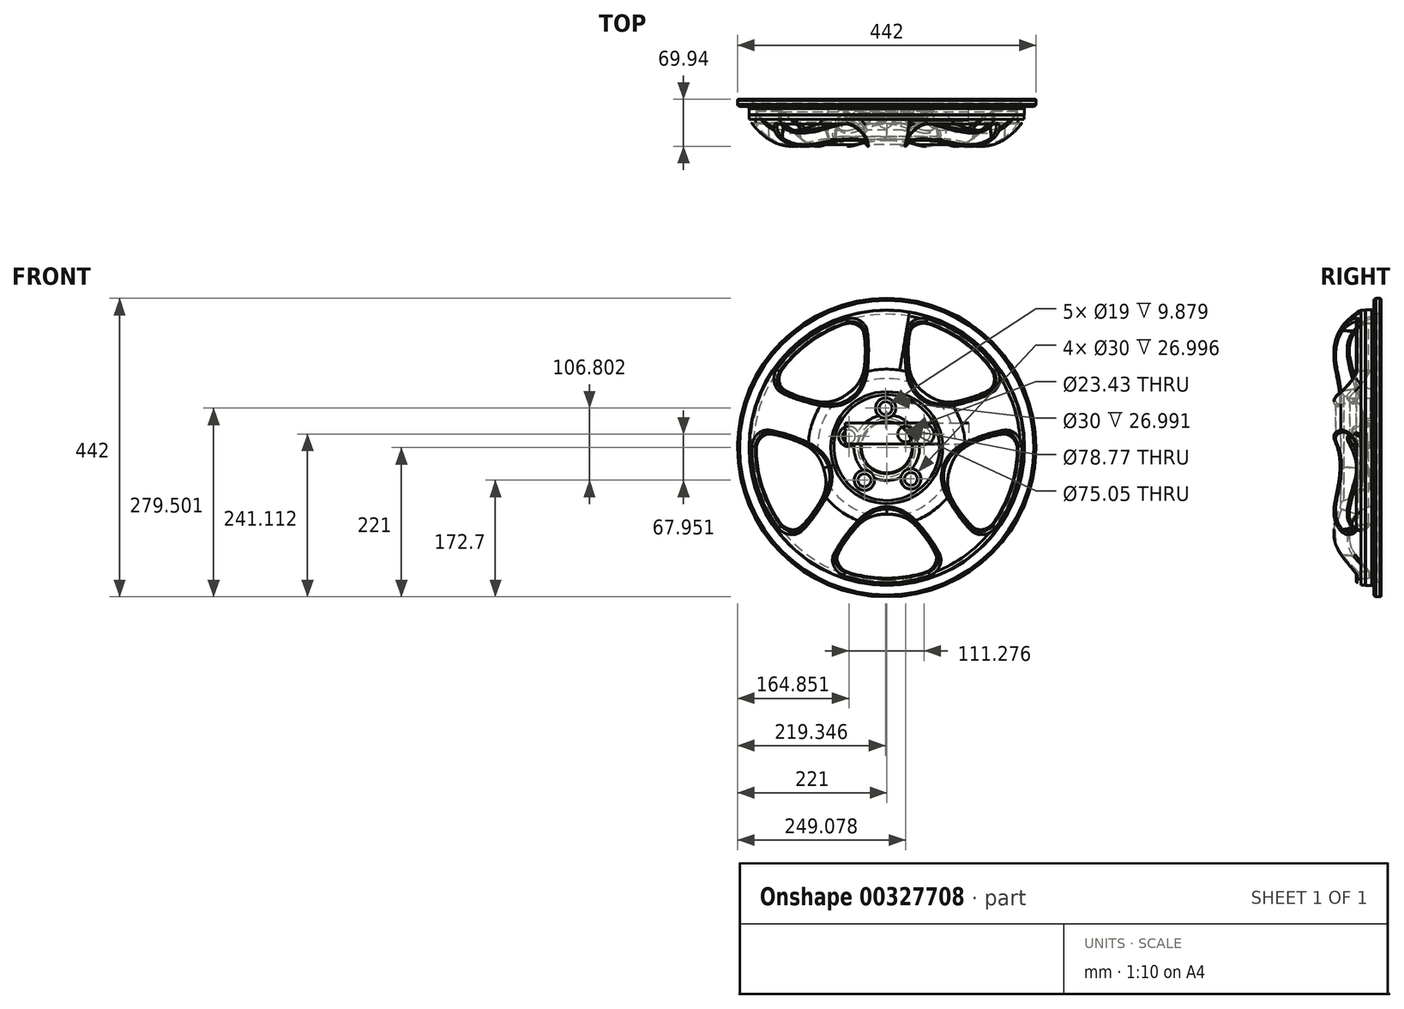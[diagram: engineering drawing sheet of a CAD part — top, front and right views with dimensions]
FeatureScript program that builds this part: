
annotation { "Feature Type Name" : "Feature", "Feature Type Description" : "" }
export const myFeature = defineFeature(function(context is Context, id is Id, definition is map)
    precondition{}
    {
        {
            var Q0;
            Q0=qCreatedBy(makeId("Right.planeOp"),FACE);
            var sketch = newSketch(context, id + "F0", { "sketchPlane" : qUnion([Q0])});
            skLineSegment(sketch, "E0", {"start": v(-299.05, 0) * mm, "end": v(298.01, 0) * mm, "construction": true});
            skLineSegment(sketch, "E1", {"start": v(-4.21, 217.93) * mm, "end": v(-4.21, 208.07) * mm});
            skFitSpline(sketch, "E2", {"points": [v(-4.21, 208.07) * mm, v(-7.55, 204.04) * mm], "startDerivative": vector(0, -5.98) * mm, "endDerivative": vector(-7.66, -0.8) * mm});
            skLineSegment(sketch, "E3", {"start": v(-7.55, 204.04) * mm, "end": v(-16.4, 204.04) * mm});
            skLineSegment(sketch, "E4", {"start": v(-16.4, 204.04) * mm, "end": v(-17.3, 203.46) * mm});
            skLineSegment(sketch, "E5", {"start": v(-17.3, 203.46) * mm, "end": v(-23.41, 203.46) * mm});
            skFitSpline(sketch, "E6", {"points": [v(-23.41, 203.46) * mm, v(-60.74, 116.16) * mm], "startDerivative": vector(-154.66, -86.95) * mm, "endDerivative": vector(7.16, -35.8) * mm});
            skLineSegment(sketch, "E7", {"start": v(-60.74, 116.16) * mm, "end": v(-53.35, 82.9) * mm});
            skFitSpline(sketch, "E8", {"points": [v(-53.35, 82.9) * mm, v(-48.78, 78.17) * mm], "startDerivative": vector(1.61, -7.86) * mm, "endDerivative": vector(6.32, -3.9) * mm});
            skFitSpline(sketch, "E9", {"points": [v(-48.78, 78.17) * mm, v(-19.88, 48.61) * mm], "startDerivative": vector(35.95, -13.03) * mm, "endDerivative": vector(3.82, -62.67) * mm});
            skLineSegment(sketch, "E10", {"start": v(-19.88, 48.61) * mm, "end": v(-19.88, 0) * mm});
            skFitSpline(sketch, "E11", {"points": [v(-4.21, 217.93) * mm, v(-1.18, 221) * mm], "startDerivative": vector(0.76, 5.98) * mm, "endDerivative": vector(4.44, 0.8) * mm});
            skLineSegment(sketch, "E12", {"start": v(-1.18, 221) * mm, "end": v(4.33, 221) * mm});
            skFitSpline(sketch, "E13", {"points": [v(4.33, 221) * mm, v(6.34, 219.66) * mm], "startDerivative": vector(2.69, 0.13) * mm, "endDerivative": vector(0.27, -2.69) * mm});
            skLineSegment(sketch, "E14", {"start": v(6.34, 219.66) * mm, "end": v(6.34, 201.82) * mm});
            skLineSegment(sketch, "E15", {"start": v(6.34, 201.82) * mm, "end": v(0, 197.57) * mm});
            skFitSpline(sketch, "E16", {"points": [v(0, 197.57) * mm, v(-39.64, 134.42) * mm], "startDerivative": vector(-50.19, -12.62) * mm, "endDerivative": vector(20.32, -117.94) * mm});
            skFitSpline(sketch, "E17", {"points": [v(-39.64, 134.42) * mm, v(-30.1, 102.27) * mm], "startDerivative": vector(9.9, -56.41) * mm, "endDerivative": vector(11.18, -25.2) * mm});
            skFitSpline(sketch, "E18", {"points": [v(-30.1, 102.27) * mm, v(-2.1, 84.7) * mm], "startDerivative": vector(23.3, -39.79) * mm, "endDerivative": vector(30.8, -8.12) * mm});
            skFitSpline(sketch, "E19", {"points": [v(-2.1, 84.7) * mm, v(0, 83.48) * mm], "startDerivative": vector(2.56, -0.67) * mm, "endDerivative": vector(0.96, -2.28) * mm});
            skLineSegment(sketch, "E20", {"start": v(0, 83.48) * mm, "end": v(0, 0) * mm});
            skLineSegment(sketch, "E21", {"start": v(0, 0) * mm, "end": v(-19.88, 0) * mm});
            skLineSegment(sketch, "E22", {"start": v(0, -290.73) * mm, "end": v(0, 298.47) * mm, "construction": true});
            skSolve(sketch);
        }
        {
            var Q0;
            Q0 = qSketchRegion(id + "F0", true);
            var Q1;
            Q1=sQuery(id+"F0.wireOp",EDGE,"E0");
            revolve(context, id + "F1", {"entities" : qUnion([Q0]), "axis" : qUnion([Q1]), "revolveType" : RevolveType.FULL});
        }
        {
            var Q0;
            Q0=qCreatedBy(makeId("Front.planeOp"),FACE);
            cPlane(context, id + "F2", {"entities" : qUnion([Q0]), "cplaneType" : CPlaneType.OFFSET, "offset" : 64.3 * mm, "width" : 150 * mm, "height" : 150 * mm});
        }
        {
            var Q0;
            Q0=qCreatedBy(makeId("Front.planeOp"),FACE);
            cPlane(context, id + "F3", {"entities" : qUnion([Q0]), "cplaneType" : CPlaneType.OFFSET, "offset" : 10 * mm, "width" : 150 * mm, "height" : 150 * mm});
        }
        {
            var Q0;
            Q0=qCreatedBy(makeId("Front.planeOp"),FACE);
            cPlane(context, id + "F4", {"entities" : qUnion([Q0]), "cplaneType" : CPlaneType.OFFSET, "offset" : 83 * mm, "width" : 150 * mm, "height" : 150 * mm});
        }
        {
            var Q0;
            Q0=qCreatedBy(makeId("Front.planeOp"),FACE);
            cPlane(context, id + "F5", {"entities" : qUnion([Q0]), "cplaneType" : CPlaneType.OFFSET, "offset" : 5 * mm, "width" : 150 * mm, "height" : 150 * mm});
        }
        {
            var Q0;
            Q0=qCreatedBy(id+"F4.planeOp",FACE);
            var sketch = newSketch(context, id + "F6", { "sketchPlane" : qUnion([Q0])});
            skLineSegment(sketch, "E23", {"start": v(-344.65, 0) * mm, "end": v(353.31, 0) * mm, "construction": true});
            skLineSegment(sketch, "E24", {"start": v(0, -300.82) * mm, "end": v(0, 297.65) * mm, "construction": true});
            skFitSpline(sketch, "E25", {"points": [v(-79, -157.26) * mm, v(-39.94, -107.29) * mm], "startDerivative": vector(39.24, 57.85) * mm, "endDerivative": vector(46.78, 52.32) * mm});
            skFitSpline(sketch, "E26", {"points": [v(-39.94, -107.29) * mm, v(0, -84.82) * mm], "startDerivative": vector(39.74, 44.77) * mm, "endDerivative": vector(30.47, -1.33) * mm});
            skFitSpline(sketch, "E27", {"points": [v(-79, -157.26) * mm, v(-77.15, -185.64) * mm], "startDerivative": vector(-20, -29.16) * mm, "endDerivative": vector(24.22, -15.46) * mm});
            skArc(sketch, "E28", {"start": v(-77.15, -185.64) * mm, "mid": v(-39.33, -197.14) * mm, "end": v(0, -201.03) * mm});
            skFitSpline(sketch, "E29.MirrorCS", {"points": [v(39.94, -107.29) * mm, v(0, -84.82) * mm], "startDerivative": vector(-39.74, 44.77) * mm, "endDerivative": vector(-30.47, -1.33) * mm});
            skFitSpline(sketch, "E30.MirrorCS", {"points": [v(79, -157.26) * mm, v(39.94, -107.29) * mm], "startDerivative": vector(-39.24, 57.85) * mm, "endDerivative": vector(-46.78, 52.32) * mm});
            skFitSpline(sketch, "E31.MirrorCS", {"points": [v(79, -157.26) * mm, v(77.15, -185.64) * mm], "startDerivative": vector(20, -29.16) * mm, "endDerivative": vector(-24.22, -15.46) * mm});
            skArc(sketch, "E32.MirrorCS", {"start": v(77.15, -185.64) * mm, "mid": v(39.33, -197.14) * mm, "end": v(0, -201.03) * mm});
            skLineSegment(sketch, "E33", {"start": v(-106.5, -327.78) * mm, "end": v(109.18, 336.02) * mm, "construction": true});
            skLineSegment(sketch, "E34", {"start": v(286.1, -92.96) * mm, "end": v(-283.08, 91.98) * mm, "construction": true});
            skFitSpline(sketch, "E35", {"points": [v(125.15, -123.74) * mm, v(89.7, -71.14) * mm], "startDerivative": vector(-42.9, 55.2) * mm, "endDerivative": vector(-35.3, 60.66) * mm});
            skFitSpline(sketch, "E36", {"points": [v(89.7, -71.14) * mm, v(80.67, -26.21) * mm], "startDerivative": vector(-30.3, 51.63) * mm, "endDerivative": vector(10.52, 31.68) * mm});
            skFitSpline(sketch, "E37", {"points": [v(125.15, -123.74) * mm, v(152.71, -130.73) * mm], "startDerivative": vector(21.56, -28.03) * mm, "endDerivative": vector(22.19, 18.26) * mm});
            skArc(sketch, "E38", {"start": v(152.71, -130.73) * mm, "mid": v(175.34, -98.33) * mm, "end": v(191.19, -62.12) * mm});
            skFitSpline(sketch, "E39.MirrorCS", {"points": [v(114.38, 4.83) * mm, v(80.67, -26.21) * mm], "startDerivative": vector(-54.86, -23.96) * mm, "endDerivative": vector(-10.11, -31.81) * mm});
            skFitSpline(sketch, "E40.MirrorCS", {"points": [v(173.98, 26.55) * mm, v(114.38, 4.83) * mm], "startDerivative": vector(-67.15, -19.44) * mm, "endDerivative": vector(-64.22, -28.33) * mm});
            skFitSpline(sketch, "E41.MirrorCS", {"points": [v(173.98, 26.55) * mm, v(200.39, 16) * mm], "startDerivative": vector(33.92, 10) * mm, "endDerivative": vector(7.22, -27.81) * mm});
            skArc(sketch, "E42.MirrorCS", {"start": v(200.39, 16) * mm, "mid": v(199.65, -23.51) * mm, "end": v(191.19, -62.12) * mm});
            skLineSegment(sketch, "E43", {"start": v(278.83, -202.58) * mm, "end": v(-285.84, 207.67) * mm, "construction": true});
            skLineSegment(sketch, "E44", {"start": v(176.82, 243.37) * mm, "end": v(-174.95, -240.8) * mm, "construction": true});
            skFitSpline(sketch, "E45", {"points": [v(156.35, 80.79) * mm, v(95.37, 63.32) * mm], "startDerivative": vector(-65.75, -23.74) * mm, "endDerivative": vector(-68.6, -14.83) * mm});
            skFitSpline(sketch, "E46", {"points": [v(95.37, 63.32) * mm, v(49.85, 68.62) * mm], "startDerivative": vector(-58.47, -12.86) * mm, "endDerivative": vector(-24.62, 18.84) * mm});
            skFitSpline(sketch, "E47", {"points": [v(156.35, 80.79) * mm, v(171.53, 104.84) * mm], "startDerivative": vector(33.32, 11.84) * mm, "endDerivative": vector(-10.5, 26.74) * mm});
            skArc(sketch, "E48", {"start": v(171.53, 104.84) * mm, "mid": v(147.7, 136.37) * mm, "end": v(118.16, 162.63) * mm});
            skFitSpline(sketch, "E49.MirrorCS", {"points": [v(30.75, 110.27) * mm, v(49.85, 68.62) * mm], "startDerivative": vector(5.84, -59.58) * mm, "endDerivative": vector(25.53, -17.6) * mm});
            skFitSpline(sketch, "E50.MirrorCS", {"points": [v(28.52, 173.67) * mm, v(30.75, 110.27) * mm], "startDerivative": vector(-2.26, -69.87) * mm, "endDerivative": vector(7.1, -69.83) * mm});
            skFitSpline(sketch, "E51.MirrorCS", {"points": [v(28.52, 173.67) * mm, v(46.7, 195.53) * mm], "startDerivative": vector(0.97, 35.35) * mm, "endDerivative": vector(28.68, -1.73) * mm});
            skArc(sketch, "E52.MirrorCS", {"start": v(46.7, 195.53) * mm, "mid": v(84.06, 182.6) * mm, "end": v(118.16, 162.63) * mm});
            skLineSegment(sketch, "E53", {"start": v(278.83, 202.58) * mm, "end": v(-285.84, -207.67) * mm, "construction": true});
            skLineSegment(sketch, "E54", {"start": v(-176.82, 243.37) * mm, "end": v(174.95, -240.8) * mm, "construction": true});
            skFitSpline(sketch, "E55", {"points": [v(-28.52, 173.67) * mm, v(-30.75, 110.27) * mm], "startDerivative": vector(2.26, -69.87) * mm, "endDerivative": vector(-7.1, -69.83) * mm});
            skFitSpline(sketch, "E56", {"points": [v(-30.75, 110.27) * mm, v(-49.85, 68.62) * mm], "startDerivative": vector(-5.84, -59.58) * mm, "endDerivative": vector(-29.1, -20.37) * mm});
            skFitSpline(sketch, "E57", {"points": [v(-28.52, 173.67) * mm, v(-46.7, 195.53) * mm], "startDerivative": vector(-0.97, 35.35) * mm, "endDerivative": vector(-28.68, -1.73) * mm});
            skArc(sketch, "E58", {"start": v(-46.7, 195.53) * mm, "mid": v(-84.06, 182.6) * mm, "end": v(-118.16, 162.63) * mm});
            skFitSpline(sketch, "E59.MirrorCS", {"points": [v(-95.37, 63.32) * mm, v(-49.85, 68.62) * mm], "startDerivative": vector(58.47, -12.86) * mm, "endDerivative": vector(28.37, 21.39) * mm});
            skFitSpline(sketch, "E60.MirrorCS", {"points": [v(-156.35, 80.79) * mm, v(-95.37, 63.32) * mm], "startDerivative": vector(65.75, -23.74) * mm, "endDerivative": vector(68.6, -14.83) * mm});
            skFitSpline(sketch, "E61.MirrorCS", {"points": [v(-156.35, 80.79) * mm, v(-171.53, 104.84) * mm], "startDerivative": vector(-33.32, 11.84) * mm, "endDerivative": vector(10.5, 26.74) * mm});
            skArc(sketch, "E62.MirrorCS", {"start": v(-171.53, 104.84) * mm, "mid": v(-147.7, 136.37) * mm, "end": v(-118.16, 162.63) * mm});
            skLineSegment(sketch, "E63", {"start": v(-106.5, 327.78) * mm, "end": v(109.18, -336.02) * mm, "construction": true});
            skLineSegment(sketch, "E64", {"start": v(-286.1, -92.96) * mm, "end": v(283.08, 91.98) * mm, "construction": true});
            skFitSpline(sketch, "E65", {"points": [v(-173.98, 26.55) * mm, v(-114.38, 4.83) * mm], "startDerivative": vector(67.15, -19.44) * mm, "endDerivative": vector(64.22, -28.33) * mm});
            skFitSpline(sketch, "E66", {"points": [v(-114.38, 4.83) * mm, v(-80.67, -26.21) * mm], "startDerivative": vector(54.86, -23.96) * mm, "endDerivative": vector(8.83, -29.97) * mm});
            skFitSpline(sketch, "E67", {"points": [v(-173.98, 26.55) * mm, v(-200.39, 16) * mm], "startDerivative": vector(-33.92, 10) * mm, "endDerivative": vector(-7.22, -27.81) * mm});
            skArc(sketch, "E68", {"start": v(-200.39, 16) * mm, "mid": v(-199.65, -23.51) * mm, "end": v(-191.19, -62.12) * mm});
            skFitSpline(sketch, "E69.MirrorCS", {"points": [v(-89.7, -71.14) * mm, v(-80.67, -26.21) * mm], "startDerivative": vector(30.3, 51.63) * mm, "endDerivative": vector(-10.47, 29.44) * mm});
            skFitSpline(sketch, "E70.MirrorCS", {"points": [v(-125.15, -123.74) * mm, v(-89.7, -71.14) * mm], "startDerivative": vector(42.9, 55.2) * mm, "endDerivative": vector(35.3, 60.66) * mm});
            skFitSpline(sketch, "E71.MirrorCS", {"points": [v(-125.15, -123.74) * mm, v(-152.71, -130.73) * mm], "startDerivative": vector(-21.56, -28.03) * mm, "endDerivative": vector(-22.19, 18.26) * mm});
            skArc(sketch, "E72.MirrorCS", {"start": v(-152.71, -130.73) * mm, "mid": v(-175.34, -98.33) * mm, "end": v(-191.19, -62.12) * mm});
            skCircle(sketch, "E73", {"center": v(0, 0) * mm, "radius": 225 * mm});
            skSolve(sketch);
        }
        {
            var Q0;
            Q0=qCreatedBy(id+"F5.planeOp",FACE);
            var sketch = newSketch(context, id + "F7", { "sketchPlane" : qUnion([Q0])});
            skFitSpline(sketch, "E74", {"points": [v(0, -103.08) * mm, v(-47.4, -124.7) * mm], "startDerivative": vector(-28.83, 0.66) * mm, "endDerivative": vector(-54.4, -62.91) * mm});
            skFitSpline(sketch, "E75", {"points": [v(-47.4, -124.7) * mm, v(-70.45, -161.6) * mm], "startDerivative": vector(-29.51, -36.76) * mm, "endDerivative": vector(-18.84, -39.87) * mm});
            skFitSpline(sketch, "E76", {"points": [v(-70.45, -161.6) * mm, v(-58.17, -183.99) * mm], "startDerivative": vector(-6.13, -31.47) * mm, "endDerivative": vector(23.73, -8.28) * mm});
            skArc(sketch, "E77", {"start": v(-58.17, -183.99) * mm, "mid": v(-29.43, -190.7) * mm, "end": v(0, -192.96) * mm});
            skFitSpline(sketch, "E78.MirrorCS", {"points": [v(0, -103.08) * mm, v(47.4, -124.7) * mm], "startDerivative": vector(28.83, 0.66) * mm, "endDerivative": vector(54.4, -62.91) * mm});
            skFitSpline(sketch, "E79.MirrorCS", {"points": [v(47.4, -124.7) * mm, v(70.45, -161.6) * mm], "startDerivative": vector(29.51, -36.76) * mm, "endDerivative": vector(18.84, -39.87) * mm});
            skFitSpline(sketch, "E80.MirrorCS", {"points": [v(70.45, -161.6) * mm, v(58.17, -183.99) * mm], "startDerivative": vector(6.13, -31.47) * mm, "endDerivative": vector(-23.73, -8.28) * mm});
            skArc(sketch, "E81.MirrorCS", {"start": v(58.17, -183.99) * mm, "mid": v(29.43, -190.7) * mm, "end": v(0, -192.96) * mm});
            skLineSegment(sketch, "E82", {"start": v(0, 310.72) * mm, "end": v(0, -319.36) * mm, "construction": true});
            skLineSegment(sketch, "E83", {"start": v(362.48, 0) * mm, "end": v(-377.5, 0) * mm, "construction": true});
            skFitSpline(sketch, "E84", {"points": [v(-98.04, -31.85) * mm, v(-133.25, 6.54) * mm], "startDerivative": vector(-8.29, 27.62) * mm, "endDerivative": vector(-76.64, 32.29) * mm});
            skFitSpline(sketch, "E85", {"points": [v(-133.25, 6.54) * mm, v(-175.46, 17.06) * mm], "startDerivative": vector(-44.08, 16.7) * mm, "endDerivative": vector(-43.74, 5.6) * mm});
            skFitSpline(sketch, "E86", {"points": [v(-175.46, 17.06) * mm, v(-192.96, -1.53) * mm], "startDerivative": vector(-31.83, -3.9) * mm, "endDerivative": vector(-0.54, -25.12) * mm});
            skArc(sketch, "E87", {"start": v(-192.96, -1.53) * mm, "mid": v(-190.46, -30.94) * mm, "end": v(-183.52, -59.63) * mm});
            skFitSpline(sketch, "E88.MirrorCS", {"points": [v(-98.04, -31.85) * mm, v(-103.96, -83.62) * mm], "startDerivative": vector(9.53, -27.22) * mm, "endDerivative": vector(-43.02, -71.17) * mm});
            skFitSpline(sketch, "E89.MirrorCS", {"points": [v(-103.96, -83.62) * mm, v(-131.92, -116.93) * mm], "startDerivative": vector(-25.84, -39.43) * mm, "endDerivative": vector(-32.1, -30.24) * mm});
            skFitSpline(sketch, "E90.MirrorCS", {"points": [v(-131.92, -116.93) * mm, v(-157, -112.18) * mm], "startDerivative": vector(-28.04, -15.56) * mm, "endDerivative": vector(-15.2, 20) * mm});
            skArc(sketch, "E91.MirrorCS", {"start": v(-157, -112.18) * mm, "mid": v(-172.28, -86.92) * mm, "end": v(-183.52, -59.63) * mm});
            skLineSegment(sketch, "E92", {"start": v(295.52, 96.02) * mm, "end": v(-303.73, -98.69) * mm, "construction": true});
            skLineSegment(sketch, "E93", {"start": v(112.01, -344.74) * mm, "end": v(-116.65, 359.02) * mm, "construction": true});
            skLineSegment(sketch, "E94.0", {"start": v(0, 0) * mm, "end": v(112.01, -344.74) * mm, "construction": true});
            skLineSegment(sketch, "E95.0", {"start": v(0, 0) * mm, "end": v(295.52, 96.02) * mm, "construction": true});
            skFitSpline(sketch, "E96", {"points": [v(98.04, -31.85) * mm, v(103.96, -83.62) * mm], "startDerivative": vector(-9.53, -27.22) * mm, "endDerivative": vector(43.02, -71.17) * mm});
            skFitSpline(sketch, "E97", {"points": [v(103.96, -83.62) * mm, v(131.92, -116.93) * mm], "startDerivative": vector(25.84, -39.43) * mm, "endDerivative": vector(32.1, -30.24) * mm});
            skFitSpline(sketch, "E98", {"points": [v(131.92, -116.93) * mm, v(157, -112.18) * mm], "startDerivative": vector(28.04, -15.56) * mm, "endDerivative": vector(15.2, 20) * mm});
            skArc(sketch, "E99", {"start": v(157, -112.18) * mm, "mid": v(172.28, -86.92) * mm, "end": v(183.52, -59.63) * mm});
            skFitSpline(sketch, "E100.MirrorCS", {"points": [v(98.04, -31.85) * mm, v(133.25, 6.54) * mm], "startDerivative": vector(8.29, 27.62) * mm, "endDerivative": vector(76.64, 32.29) * mm});
            skFitSpline(sketch, "E101.MirrorCS", {"points": [v(133.25, 6.54) * mm, v(175.46, 17.06) * mm], "startDerivative": vector(44.08, 16.7) * mm, "endDerivative": vector(43.74, 5.6) * mm});
            skFitSpline(sketch, "E102.MirrorCS", {"points": [v(175.46, 17.06) * mm, v(192.96, -1.53) * mm], "startDerivative": vector(31.83, -3.9) * mm, "endDerivative": vector(0.54, -25.12) * mm});
            skArc(sketch, "E103.MirrorCS", {"start": v(192.96, -1.53) * mm, "mid": v(190.46, -30.94) * mm, "end": v(183.52, -59.63) * mm});
            skLineSegment(sketch, "E104", {"start": v(-295.52, 96.02) * mm, "end": v(303.73, -98.69) * mm, "construction": true});
            skLineSegment(sketch, "E105", {"start": v(112.01, 344.74) * mm, "end": v(-116.65, -359.02) * mm, "construction": true});
            skLineSegment(sketch, "E106.0", {"start": v(0, 0) * mm, "end": v(112.01, 344.74) * mm, "construction": true});
            skLineSegment(sketch, "E107.0", {"start": v(0, 0) * mm, "end": v(-295.52, 96.02) * mm, "construction": true});
            skFitSpline(sketch, "E108", {"points": [v(60.6, 83.4) * mm, v(111.65, 73.03) * mm], "startDerivative": vector(22.94, -17.48) * mm, "endDerivative": vector(80.98, 18.93) * mm});
            skFitSpline(sketch, "E109", {"points": [v(111.65, 73.03) * mm, v(151.98, 89.33) * mm], "startDerivative": vector(45.49, 12.4) * mm, "endDerivative": vector(38.68, 21.18) * mm});
            skFitSpline(sketch, "E110", {"points": [v(151.98, 89.33) * mm, v(155.2, 114.66) * mm], "startDerivative": vector(23.46, 21.86) * mm, "endDerivative": vector(-14.33, 20.64) * mm});
            skArc(sketch, "E111", {"start": v(155.2, 114.66) * mm, "mid": v(135.9, 136.99) * mm, "end": v(113.42, 156.1) * mm});
            skFitSpline(sketch, "E112.MirrorCS", {"points": [v(60.6, 83.4) * mm, v(34.95, 128.75) * mm], "startDerivative": vector(-23.7, 16.42) * mm, "endDerivative": vector(-7.03, 82.87) * mm});
            skFitSpline(sketch, "E113.MirrorCS", {"points": [v(34.95, 128.75) * mm, v(38, 172.14) * mm], "startDerivative": vector(-2.27, 47.09) * mm, "endDerivative": vector(8.2, 43.33) * mm});
            skFitSpline(sketch, "E114.MirrorCS", {"points": [v(38, 172.14) * mm, v(61.08, 183.04) * mm], "startDerivative": vector(13.54, 29.07) * mm, "endDerivative": vector(24.06, -7.25) * mm});
            skArc(sketch, "E115.MirrorCS", {"start": v(61.08, 183.04) * mm, "mid": v(88.29, 171.58) * mm, "end": v(113.42, 156.1) * mm});
            skLineSegment(sketch, "E116", {"start": v(-182.64, -251.38) * mm, "end": v(187.71, 258.37) * mm, "construction": true});
            skLineSegment(sketch, "E117", {"start": v(-293.25, 213.06) * mm, "end": v(305.4, -221.88) * mm, "construction": true});
            skLineSegment(sketch, "E118.0", {"start": v(0, 0) * mm, "end": v(-293.25, 213.06) * mm, "construction": true});
            skLineSegment(sketch, "E119.0", {"start": v(0, 0) * mm, "end": v(-182.64, -251.38) * mm, "construction": true});
            skFitSpline(sketch, "E120", {"points": [v(-60.6, 83.4) * mm, v(-34.95, 128.75) * mm], "startDerivative": vector(23.7, 16.42) * mm, "endDerivative": vector(7.03, 82.87) * mm});
            skFitSpline(sketch, "E121", {"points": [v(-34.95, 128.75) * mm, v(-38, 172.14) * mm], "startDerivative": vector(2.27, 47.09) * mm, "endDerivative": vector(-8.2, 43.33) * mm});
            skFitSpline(sketch, "E122", {"points": [v(-38, 172.14) * mm, v(-61.08, 183.04) * mm], "startDerivative": vector(-13.54, 29.07) * mm, "endDerivative": vector(-24.06, -7.25) * mm});
            skArc(sketch, "E123", {"start": v(-61.08, 183.04) * mm, "mid": v(-88.29, 171.58) * mm, "end": v(-113.42, 156.1) * mm});
            skFitSpline(sketch, "E124.MirrorCS", {"points": [v(-60.6, 83.4) * mm, v(-111.65, 73.03) * mm], "startDerivative": vector(-22.94, -17.48) * mm, "endDerivative": vector(-80.98, 18.93) * mm});
            skFitSpline(sketch, "E125.MirrorCS", {"points": [v(-111.65, 73.03) * mm, v(-151.98, 89.33) * mm], "startDerivative": vector(-45.49, 12.4) * mm, "endDerivative": vector(-38.68, 21.18) * mm});
            skFitSpline(sketch, "E126.MirrorCS", {"points": [v(-151.98, 89.33) * mm, v(-155.2, 114.66) * mm], "startDerivative": vector(-23.46, 21.86) * mm, "endDerivative": vector(14.33, 20.64) * mm});
            skArc(sketch, "E127.MirrorCS", {"start": v(-155.2, 114.66) * mm, "mid": v(-135.9, 136.99) * mm, "end": v(-113.42, 156.1) * mm});
            skLineSegment(sketch, "E128", {"start": v(182.64, -251.38) * mm, "end": v(-187.71, 258.37) * mm, "construction": true});
            skLineSegment(sketch, "E129", {"start": v(-293.25, -213.06) * mm, "end": v(305.4, 221.88) * mm, "construction": true});
            skLineSegment(sketch, "E130.0", {"start": v(0, 0) * mm, "end": v(-293.25, -213.06) * mm, "construction": true});
            skLineSegment(sketch, "E131.0", {"start": v(0, 0) * mm, "end": v(182.64, -251.38) * mm, "construction": true});
            skCircle(sketch, "E132", {"center": v(0, 0) * mm, "radius": 225 * mm});
            skSolve(sketch);
        }
        {
            var Q1;
            Q1=makeQuery(id+"F6.imprint","IMPRINT",FACE,{"disambiguationData":[TD([[makeQuery(id+"F6.imprint","IMPRINT",EDGE,{"derivedFrom":sQuery(id+"F6.wireOp",EDGE,"E25")}),-1.0]])]});
            var Q2;
            Q2=makeQuery(id+"F7.imprint","IMPRINT",FACE,{"disambiguationData":[TD([[makeQuery(id+"F7.imprint","IMPRINT",EDGE,{"derivedFrom":sQuery(id+"F7.wireOp",EDGE,"E74")}),1.0]])]});
            var Q3;
            Q3=sQuery(id+"F6.wireOp",VERTEX,"E26.end");
            var Q4;
            Q4=sQuery(id+"F6.wireOp",VERTEX,"E26.start");
            var Q5;
            Q5=sQuery(id+"F6.wireOp",VERTEX,"E27.start");
            var Q6;
            Q6=sQuery(id+"F6.wireOp",VERTEX,"E28.start");
            var Q7;
            Q7=sQuery(id+"F6.wireOp",VERTEX,"E28.end");
            var Q8;
            Q8=sQuery(id+"F6.wireOp",VERTEX,"E31.MirrorCS.1.internal");
            var Q9;
            Q9=sQuery(id+"F6.wireOp",VERTEX,"E30.MirrorCS.start");
            var Q10;
            Q10=sQuery(id+"F6.wireOp",VERTEX,"E29.MirrorCS.start");
            var Q11;
            Q11=sQuery(id+"F7.wireOp",VERTEX,"E74.start");
            var Q12;
            Q12=sQuery(id+"F7.wireOp",VERTEX,"E79.MirrorCS.0.internal");
            var Q13;
            Q13=sQuery(id+"F7.wireOp",VERTEX,"E80.MirrorCS.0.internal");
            var Q14;
            Q14=sQuery(id+"F7.wireOp",VERTEX,"E77.end");
            var Q15;
            Q15=sQuery(id+"F7.wireOp",VERTEX,"E77.start");
            var Q16;
            Q16=sQuery(id+"F7.wireOp",VERTEX,"E76.start");
            var Q17;
            Q17=sQuery(id+"F7.wireOp",VERTEX,"E75.start");
            loft(context, id + "F8", {"operationType" : NewBodyOperationType.REMOVE, "startCondition" : LoftEndDerivativeType.NORMAL_TO_PROFILE, "startMagnitude" : 1, "endCondition" : LoftEndDerivativeType.NORMAL_TO_PROFILE, "endMagnitude" : 1, "sheetProfilesArray" : [{ "sheetProfileEntities" : qUnion([Q1]) }, { "sheetProfileEntities" : qUnion([Q2]) }], "connections" : [{ "connectionEntities" : qUnion([Q3, Q4, Q5, Q6, Q7, Q8, Q9, Q10, Q11, Q12, Q13, Q14, Q15, Q16, Q17]), "connectionEdgeQueries" : qUnion([]), "connectionEdgeParameters" : [] }]});
        }
        {
            var Q1;
            Q1=makeQuery(id+"F6.imprint","IMPRINT",FACE,{"disambiguationData":[TD([[makeQuery(id+"F6.imprint","IMPRINT",EDGE,{"derivedFrom":sQuery(id+"F6.wireOp",EDGE,"E65")}),-1.0]])]});
            var Q2;
            Q2=makeQuery(id+"F7.imprint","IMPRINT",FACE,{"disambiguationData":[TD([[makeQuery(id+"F7.imprint","IMPRINT",EDGE,{"derivedFrom":sQuery(id+"F7.wireOp",EDGE,"E84")}),1.0]])]});
            loft(context, id + "F9", {"operationType" : NewBodyOperationType.REMOVE, "startCondition" : LoftEndDerivativeType.NORMAL_TO_PROFILE, "startMagnitude" : 1, "endCondition" : LoftEndDerivativeType.NORMAL_TO_PROFILE, "endMagnitude" : 1, "sheetProfilesArray" : [{ "sheetProfileEntities" : qUnion([Q1]) }, { "sheetProfileEntities" : qUnion([Q2]) }]});
        }
        {
            var Q1;
            Q1=makeQuery(id+"F6.imprint","IMPRINT",FACE,{"disambiguationData":[TD([[makeQuery(id+"F6.imprint","IMPRINT",EDGE,{"derivedFrom":sQuery(id+"F6.wireOp",EDGE,"E55")}),-1.0]])]});
            var Q2;
            Q2=makeQuery(id+"F7.imprint","IMPRINT",FACE,{"disambiguationData":[TD([[makeQuery(id+"F7.imprint","IMPRINT",EDGE,{"derivedFrom":sQuery(id+"F7.wireOp",EDGE,"E120")}),1.0]])]});
            loft(context, id + "F10", {"operationType" : NewBodyOperationType.REMOVE, "startCondition" : LoftEndDerivativeType.NORMAL_TO_PROFILE, "startMagnitude" : 1, "endCondition" : LoftEndDerivativeType.NORMAL_TO_PROFILE, "endMagnitude" : 1, "sheetProfilesArray" : [{ "sheetProfileEntities" : qUnion([Q1]) }, { "sheetProfileEntities" : qUnion([Q2]) }]});
        }
        {
            var Q1;
            Q1=makeQuery(id+"F6.imprint","IMPRINT",FACE,{"disambiguationData":[TD([[makeQuery(id+"F6.imprint","IMPRINT",EDGE,{"derivedFrom":sQuery(id+"F6.wireOp",EDGE,"E45")}),-1.0]])]});
            var Q2;
            Q2=makeQuery(id+"F7.imprint","IMPRINT",FACE,{"disambiguationData":[TD([[makeQuery(id+"F7.imprint","IMPRINT",EDGE,{"derivedFrom":sQuery(id+"F7.wireOp",EDGE,"E108")}),1.0]])]});
            loft(context, id + "F11", {"operationType" : NewBodyOperationType.REMOVE, "startCondition" : LoftEndDerivativeType.NORMAL_TO_PROFILE, "startMagnitude" : 1, "endCondition" : LoftEndDerivativeType.NORMAL_TO_PROFILE, "endMagnitude" : 1, "sheetProfilesArray" : [{ "sheetProfileEntities" : qUnion([Q1]) }, { "sheetProfileEntities" : qUnion([Q2]) }]});
        }
        {
            var Q1;
            Q1=makeQuery(id+"F6.imprint","IMPRINT",FACE,{"disambiguationData":[TD([[makeQuery(id+"F6.imprint","IMPRINT",EDGE,{"derivedFrom":sQuery(id+"F6.wireOp",EDGE,"E35")}),-1.0]])]});
            var Q2;
            Q2=makeQuery(id+"F7.imprint","IMPRINT",FACE,{"disambiguationData":[TD([[makeQuery(id+"F7.imprint","IMPRINT",EDGE,{"derivedFrom":sQuery(id+"F7.wireOp",EDGE,"E96")}),1.0]])]});
            loft(context, id + "F12", {"operationType" : NewBodyOperationType.REMOVE, "startCondition" : LoftEndDerivativeType.NORMAL_TO_PROFILE, "startMagnitude" : 1, "endCondition" : LoftEndDerivativeType.NORMAL_TO_PROFILE, "endMagnitude" : 1, "sheetProfilesArray" : [{ "sheetProfileEntities" : qUnion([Q1]) }, { "sheetProfileEntities" : qUnion([Q2]) }]});
        }
        {
            var Q0;
            Q0=qCreatedBy(id+"F2.planeOp",FACE);
            var sketch = newSketch(context, id + "F13", { "sketchPlane" : qUnion([Q0])});
            skCircle(sketch, "E133.cCircle", {"center": v(0, 0) * mm, "radius": 47.35 * mm, "construction": true});
            skLineSegment(sketch, "E133.0", {"start": v(-56.15, 16.5) * mm, "end": v(-1.65, 58.5) * mm, "construction": true});
            skLineSegment(sketch, "E133.1", {"start": v(-1.65, 58.5) * mm, "end": v(55.13, 19.65) * mm, "construction": true});
            skLineSegment(sketch, "E133.2", {"start": v(55.13, 19.65) * mm, "end": v(35.72, -46.36) * mm, "construction": true});
            skLineSegment(sketch, "E133.3", {"start": v(35.72, -46.36) * mm, "end": v(-33.05, -48.3) * mm, "construction": true});
            skLineSegment(sketch, "E133.4", {"start": v(-33.05, -48.3) * mm, "end": v(-56.15, 16.5) * mm, "construction": true});
            skPoint(sketch, "E133.0.midPoint", {"position": v(-28.9, 37.5) * mm});
            skSolve(sketch);
        }
        {
            var Q0;
            Q0=sQuery(id+"F13.wireOp",VERTEX,"E133.1.start");
            var Q1;
            Q1=sQuery(id+"F13.wireOp",VERTEX,"E133.0.start");
            var Q2;
            Q2=sQuery(id+"F13.wireOp",VERTEX,"E133.4.start");
            var Q3;
            Q3=sQuery(id+"F13.wireOp",VERTEX,"E133.2.end");
            var Q4;
            Q4=sQuery(id+"F13.wireOp",VERTEX,"E133.2.start");
            var Q5;
            Q5=makeQuery(id+"F1.opRevolve","SWEPT_BODY",BODY,{"disambiguationData":[OSD([sQuery(id+"F0.wireOp",EDGE,"E1"),sQuery(id+"F0.wireOp",EDGE,"E2"),sQuery(id+"F0.wireOp",EDGE,"E3"),sQuery(id+"F0.wireOp",EDGE,"E4"),sQuery(id+"F0.wireOp",EDGE,"E5"),sQuery(id+"F0.wireOp",EDGE,"E6"),sQuery(id+"F0.wireOp",EDGE,"E7"),sQuery(id+"F0.wireOp",EDGE,"E8"),sQuery(id+"F0.wireOp",EDGE,"E9"),sQuery(id+"F0.wireOp",EDGE,"E10"),sQuery(id+"F0.wireOp",EDGE,"E11"),sQuery(id+"F0.wireOp",EDGE,"E12"),sQuery(id+"F0.wireOp",EDGE,"E13"),sQuery(id+"F0.wireOp",EDGE,"E14"),sQuery(id+"F0.wireOp",EDGE,"E15"),sQuery(id+"F0.wireOp",EDGE,"E16"),sQuery(id+"F0.wireOp",EDGE,"E17"),sQuery(id+"F0.wireOp",EDGE,"E18"),sQuery(id+"F0.wireOp",EDGE,"E19"),sQuery(id+"F0.wireOp",EDGE,"E20"),sQuery(id+"F0.wireOp",EDGE,"E21")])]});
            hole(context, id + "F14", {"style" : HoleStyle.C_BORE, "endStyle" : HoleEndStyle.BLIND, "holeDiameter" : 19 * mm, "cBoreDiameter" : 30 * mm, "cBoreDepth" : 10 * mm, "holeDepth" : 50 * mm, "tappedDepth" : 12 * mm, "tapClearance" : 3, "locations" : qUnion([Q0, Q1, Q2, Q3, Q4]), "scope" : qUnion([Q5]), "startStyle" : HoleStartStyle.PART});
        }
        {
            var Q0;
            Q0=makeQuery(id+"F9.boolean.opBoolean","COPY",FACE,{"derivedFrom":makeQuery(id+"F9.opLoft","SWEPT_FACE",FACE,{"disambiguationData":[OSD([sQuery(id+"F6.wireOp",EDGE,"E66"),sQuery(id+"F6.wireOp",EDGE,"E69.MirrorCS"),sQuery(id+"F6.wireOp",EDGE,"E70.MirrorCS"),sQuery(id+"F7.wireOp",EDGE,"E84"),sQuery(id+"F7.wireOp",EDGE,"E88.MirrorCS"),sQuery(id+"F7.wireOp",EDGE,"E89.MirrorCS")])]})});
            var Q1;
            Q1=makeQuery(id+"F9.boolean.opBoolean","COPY",FACE,{"derivedFrom":makeQuery(id+"F9.opLoft","SWEPT_FACE",FACE,{"disambiguationData":[OSD([sQuery(id+"F6.wireOp",EDGE,"E65"),sQuery(id+"F6.wireOp",EDGE,"E66"),sQuery(id+"F6.wireOp",EDGE,"E69.MirrorCS"),sQuery(id+"F7.wireOp",EDGE,"E84"),sQuery(id+"F7.wireOp",EDGE,"E85"),sQuery(id+"F7.wireOp",EDGE,"E88.MirrorCS")])]})});
            var Q2;
            Q2=makeQuery(id+"F9.boolean.opBoolean","COPY",FACE,{"derivedFrom":makeQuery(id+"F9.opLoft","SWEPT_FACE",FACE,{"disambiguationData":[OSD([sQuery(id+"F6.wireOp",EDGE,"E65"),sQuery(id+"F6.wireOp",EDGE,"E66"),sQuery(id+"F6.wireOp",EDGE,"E67"),sQuery(id+"F7.wireOp",EDGE,"E84"),sQuery(id+"F7.wireOp",EDGE,"E85"),sQuery(id+"F7.wireOp",EDGE,"E86")])]})});
            var Q3;
            Q3=makeQuery(id+"F9.boolean.opBoolean","COPY",FACE,{"derivedFrom":makeQuery(id+"F9.opLoft","SWEPT_FACE",FACE,{"disambiguationData":[OSD([sQuery(id+"F6.wireOp",EDGE,"E65"),sQuery(id+"F6.wireOp",EDGE,"E67"),sQuery(id+"F6.wireOp",EDGE,"E68"),sQuery(id+"F7.wireOp",EDGE,"E85"),sQuery(id+"F7.wireOp",EDGE,"E86"),sQuery(id+"F7.wireOp",EDGE,"E87")])]})});
            var Q4;
            Q4=makeQuery(id+"F9.boolean.opBoolean","COPY",FACE,{"derivedFrom":makeQuery(id+"F9.opLoft","SWEPT_FACE",FACE,{"disambiguationData":[OSD([sQuery(id+"F6.wireOp",EDGE,"E69.MirrorCS"),sQuery(id+"F6.wireOp",EDGE,"E70.MirrorCS"),sQuery(id+"F6.wireOp",EDGE,"E71.MirrorCS"),sQuery(id+"F7.wireOp",EDGE,"E88.MirrorCS"),sQuery(id+"F7.wireOp",EDGE,"E89.MirrorCS"),sQuery(id+"F7.wireOp",EDGE,"E90.MirrorCS")])]})});
            var Q5;
            Q5=makeQuery(id+"F9.boolean.opBoolean","COPY",FACE,{"derivedFrom":makeQuery(id+"F9.opLoft","SWEPT_FACE",FACE,{"disambiguationData":[OSD([sQuery(id+"F6.wireOp",EDGE,"E70.MirrorCS"),sQuery(id+"F6.wireOp",EDGE,"E71.MirrorCS"),sQuery(id+"F6.wireOp",EDGE,"E72.MirrorCS"),sQuery(id+"F7.wireOp",EDGE,"E89.MirrorCS"),sQuery(id+"F7.wireOp",EDGE,"E90.MirrorCS"),sQuery(id+"F7.wireOp",EDGE,"E91.MirrorCS")])]})});
            var Q6;
            Q6=makeQuery(id+"F9.boolean.opBoolean","COPY",FACE,{"derivedFrom":makeQuery(id+"F9.opLoft","SWEPT_FACE",FACE,{"disambiguationData":[OSD([sQuery(id+"F6.wireOp",EDGE,"E68"),sQuery(id+"F6.wireOp",EDGE,"E71.MirrorCS"),sQuery(id+"F6.wireOp",EDGE,"E72.MirrorCS"),sQuery(id+"F7.wireOp",EDGE,"E87"),sQuery(id+"F7.wireOp",EDGE,"E90.MirrorCS"),sQuery(id+"F7.wireOp",EDGE,"E91.MirrorCS")])]})});
            var Q7;
            Q7=makeQuery(id+"F10.boolean.opBoolean","COPY",FACE,{"derivedFrom":makeQuery(id+"F10.opLoft","SWEPT_FACE",FACE,{"disambiguationData":[OSD([sQuery(id+"F6.wireOp",EDGE,"E60.MirrorCS"),sQuery(id+"F6.wireOp",EDGE,"E61.MirrorCS"),sQuery(id+"F6.wireOp",EDGE,"E62.MirrorCS"),sQuery(id+"F7.wireOp",EDGE,"E125.MirrorCS"),sQuery(id+"F7.wireOp",EDGE,"E126.MirrorCS"),sQuery(id+"F7.wireOp",EDGE,"E127.MirrorCS")])]})});
            var Q8;
            Q8=makeQuery(id+"F10.boolean.opBoolean","COPY",FACE,{"derivedFrom":makeQuery(id+"F10.opLoft","SWEPT_FACE",FACE,{"disambiguationData":[OSD([sQuery(id+"F6.wireOp",EDGE,"E58"),sQuery(id+"F6.wireOp",EDGE,"E61.MirrorCS"),sQuery(id+"F6.wireOp",EDGE,"E62.MirrorCS"),sQuery(id+"F7.wireOp",EDGE,"E123"),sQuery(id+"F7.wireOp",EDGE,"E126.MirrorCS"),sQuery(id+"F7.wireOp",EDGE,"E127.MirrorCS")])]})});
            var Q9;
            Q9=makeQuery(id+"F10.boolean.opBoolean","COPY",FACE,{"derivedFrom":makeQuery(id+"F10.opLoft","SWEPT_FACE",FACE,{"disambiguationData":[OSD([sQuery(id+"F6.wireOp",EDGE,"E59.MirrorCS"),sQuery(id+"F6.wireOp",EDGE,"E60.MirrorCS"),sQuery(id+"F6.wireOp",EDGE,"E61.MirrorCS"),sQuery(id+"F7.wireOp",EDGE,"E124.MirrorCS"),sQuery(id+"F7.wireOp",EDGE,"E125.MirrorCS"),sQuery(id+"F7.wireOp",EDGE,"E126.MirrorCS")])]})});
            var Q10;
            Q10=makeQuery(id+"F10.boolean.opBoolean","COPY",FACE,{"derivedFrom":makeQuery(id+"F10.opLoft","SWEPT_FACE",FACE,{"disambiguationData":[OSD([sQuery(id+"F6.wireOp",EDGE,"E56"),sQuery(id+"F6.wireOp",EDGE,"E59.MirrorCS"),sQuery(id+"F6.wireOp",EDGE,"E60.MirrorCS"),sQuery(id+"F7.wireOp",EDGE,"E120"),sQuery(id+"F7.wireOp",EDGE,"E124.MirrorCS"),sQuery(id+"F7.wireOp",EDGE,"E125.MirrorCS")])]})});
            var Q11;
            Q11=makeQuery(id+"F10.boolean.opBoolean","COPY",FACE,{"derivedFrom":makeQuery(id+"F10.opLoft","SWEPT_FACE",FACE,{"disambiguationData":[OSD([sQuery(id+"F6.wireOp",EDGE,"E55"),sQuery(id+"F6.wireOp",EDGE,"E56"),sQuery(id+"F6.wireOp",EDGE,"E59.MirrorCS"),sQuery(id+"F7.wireOp",EDGE,"E120"),sQuery(id+"F7.wireOp",EDGE,"E121"),sQuery(id+"F7.wireOp",EDGE,"E124.MirrorCS")])]})});
            var Q12;
            Q12=makeQuery(id+"F10.boolean.opBoolean","COPY",FACE,{"derivedFrom":makeQuery(id+"F10.opLoft","SWEPT_FACE",FACE,{"disambiguationData":[OSD([sQuery(id+"F6.wireOp",EDGE,"E55"),sQuery(id+"F6.wireOp",EDGE,"E56"),sQuery(id+"F6.wireOp",EDGE,"E57"),sQuery(id+"F7.wireOp",EDGE,"E120"),sQuery(id+"F7.wireOp",EDGE,"E121"),sQuery(id+"F7.wireOp",EDGE,"E122")])]})});
            var Q13;
            Q13=makeQuery(id+"F10.boolean.opBoolean","COPY",FACE,{"derivedFrom":makeQuery(id+"F10.opLoft","SWEPT_FACE",FACE,{"disambiguationData":[OSD([sQuery(id+"F6.wireOp",EDGE,"E55"),sQuery(id+"F6.wireOp",EDGE,"E57"),sQuery(id+"F6.wireOp",EDGE,"E58"),sQuery(id+"F7.wireOp",EDGE,"E121"),sQuery(id+"F7.wireOp",EDGE,"E122"),sQuery(id+"F7.wireOp",EDGE,"E123")])]})});
            var Q14;
            Q14=makeQuery(id+"F11.boolean.opBoolean","COPY",FACE,{"derivedFrom":makeQuery(id+"F11.opLoft","SWEPT_FACE",FACE,{"disambiguationData":[OSD([sQuery(id+"F6.wireOp",EDGE,"E48"),sQuery(id+"F6.wireOp",EDGE,"E51.MirrorCS"),sQuery(id+"F6.wireOp",EDGE,"E52.MirrorCS"),sQuery(id+"F7.wireOp",EDGE,"E111"),sQuery(id+"F7.wireOp",EDGE,"E114.MirrorCS"),sQuery(id+"F7.wireOp",EDGE,"E115.MirrorCS")])]})});
            var Q15;
            Q15=makeQuery(id+"F11.boolean.opBoolean","COPY",FACE,{"derivedFrom":makeQuery(id+"F11.opLoft","SWEPT_FACE",FACE,{"disambiguationData":[OSD([sQuery(id+"F6.wireOp",EDGE,"E45"),sQuery(id+"F6.wireOp",EDGE,"E47"),sQuery(id+"F6.wireOp",EDGE,"E48"),sQuery(id+"F7.wireOp",EDGE,"E109"),sQuery(id+"F7.wireOp",EDGE,"E110"),sQuery(id+"F7.wireOp",EDGE,"E111")])]})});
            var Q16;
            Q16=makeQuery(id+"F11.boolean.opBoolean","COPY",FACE,{"derivedFrom":makeQuery(id+"F11.opLoft","SWEPT_FACE",FACE,{"disambiguationData":[OSD([sQuery(id+"F6.wireOp",EDGE,"E45"),sQuery(id+"F6.wireOp",EDGE,"E46"),sQuery(id+"F6.wireOp",EDGE,"E47"),sQuery(id+"F7.wireOp",EDGE,"E108"),sQuery(id+"F7.wireOp",EDGE,"E109"),sQuery(id+"F7.wireOp",EDGE,"E110")])]})});
            var Q17;
            Q17=makeQuery(id+"F11.boolean.opBoolean","COPY",FACE,{"derivedFrom":makeQuery(id+"F11.opLoft","SWEPT_FACE",FACE,{"disambiguationData":[OSD([sQuery(id+"F6.wireOp",EDGE,"E45"),sQuery(id+"F6.wireOp",EDGE,"E46"),sQuery(id+"F6.wireOp",EDGE,"E49.MirrorCS"),sQuery(id+"F7.wireOp",EDGE,"E108"),sQuery(id+"F7.wireOp",EDGE,"E109"),sQuery(id+"F7.wireOp",EDGE,"E112.MirrorCS")])]})});
            var Q18;
            Q18=makeQuery(id+"F11.boolean.opBoolean","COPY",FACE,{"derivedFrom":makeQuery(id+"F11.opLoft","SWEPT_FACE",FACE,{"disambiguationData":[OSD([sQuery(id+"F6.wireOp",EDGE,"E46"),sQuery(id+"F6.wireOp",EDGE,"E49.MirrorCS"),sQuery(id+"F6.wireOp",EDGE,"E50.MirrorCS"),sQuery(id+"F7.wireOp",EDGE,"E108"),sQuery(id+"F7.wireOp",EDGE,"E112.MirrorCS"),sQuery(id+"F7.wireOp",EDGE,"E113.MirrorCS")])]})});
            var Q19;
            Q19=makeQuery(id+"F11.boolean.opBoolean","COPY",FACE,{"derivedFrom":makeQuery(id+"F11.opLoft","SWEPT_FACE",FACE,{"disambiguationData":[OSD([sQuery(id+"F6.wireOp",EDGE,"E49.MirrorCS"),sQuery(id+"F6.wireOp",EDGE,"E50.MirrorCS"),sQuery(id+"F6.wireOp",EDGE,"E51.MirrorCS"),sQuery(id+"F7.wireOp",EDGE,"E112.MirrorCS"),sQuery(id+"F7.wireOp",EDGE,"E113.MirrorCS"),sQuery(id+"F7.wireOp",EDGE,"E114.MirrorCS")])]})});
            var Q20;
            Q20=makeQuery(id+"F11.boolean.opBoolean","COPY",FACE,{"derivedFrom":makeQuery(id+"F11.opLoft","SWEPT_FACE",FACE,{"disambiguationData":[OSD([sQuery(id+"F6.wireOp",EDGE,"E50.MirrorCS"),sQuery(id+"F6.wireOp",EDGE,"E51.MirrorCS"),sQuery(id+"F6.wireOp",EDGE,"E52.MirrorCS"),sQuery(id+"F7.wireOp",EDGE,"E113.MirrorCS"),sQuery(id+"F7.wireOp",EDGE,"E114.MirrorCS"),sQuery(id+"F7.wireOp",EDGE,"E115.MirrorCS")])]})});
            var Q21;
            Q21=makeQuery(id+"F12.boolean.opBoolean","COPY",FACE,{"derivedFrom":makeQuery(id+"F12.opLoft","SWEPT_FACE",FACE,{"disambiguationData":[OSD([sQuery(id+"F6.wireOp",EDGE,"E35"),sQuery(id+"F6.wireOp",EDGE,"E36"),sQuery(id+"F6.wireOp",EDGE,"E37"),sQuery(id+"F7.wireOp",EDGE,"E96"),sQuery(id+"F7.wireOp",EDGE,"E97"),sQuery(id+"F7.wireOp",EDGE,"E98")])]})});
            var Q22;
            Q22=makeQuery(id+"F12.boolean.opBoolean","COPY",FACE,{"derivedFrom":makeQuery(id+"F12.opLoft","SWEPT_FACE",FACE,{"disambiguationData":[OSD([sQuery(id+"F6.wireOp",EDGE,"E35"),sQuery(id+"F6.wireOp",EDGE,"E36"),sQuery(id+"F6.wireOp",EDGE,"E39.MirrorCS"),sQuery(id+"F7.wireOp",EDGE,"E96"),sQuery(id+"F7.wireOp",EDGE,"E97"),sQuery(id+"F7.wireOp",EDGE,"E100.MirrorCS")])]})});
            var Q23;
            Q23=makeQuery(id+"F12.boolean.opBoolean","COPY",FACE,{"derivedFrom":makeQuery(id+"F12.opLoft","SWEPT_FACE",FACE,{"disambiguationData":[OSD([sQuery(id+"F6.wireOp",EDGE,"E36"),sQuery(id+"F6.wireOp",EDGE,"E39.MirrorCS"),sQuery(id+"F6.wireOp",EDGE,"E40.MirrorCS"),sQuery(id+"F7.wireOp",EDGE,"E96"),sQuery(id+"F7.wireOp",EDGE,"E100.MirrorCS"),sQuery(id+"F7.wireOp",EDGE,"E101.MirrorCS")])]})});
            var Q24;
            Q24=makeQuery(id+"F12.boolean.opBoolean","COPY",FACE,{"derivedFrom":makeQuery(id+"F12.opLoft","SWEPT_FACE",FACE,{"disambiguationData":[OSD([sQuery(id+"F6.wireOp",EDGE,"E39.MirrorCS"),sQuery(id+"F6.wireOp",EDGE,"E40.MirrorCS"),sQuery(id+"F6.wireOp",EDGE,"E41.MirrorCS"),sQuery(id+"F7.wireOp",EDGE,"E100.MirrorCS"),sQuery(id+"F7.wireOp",EDGE,"E101.MirrorCS"),sQuery(id+"F7.wireOp",EDGE,"E102.MirrorCS")])]})});
            var Q25;
            Q25=makeQuery(id+"F12.boolean.opBoolean","COPY",FACE,{"derivedFrom":makeQuery(id+"F12.opLoft","SWEPT_FACE",FACE,{"disambiguationData":[OSD([sQuery(id+"F6.wireOp",EDGE,"E40.MirrorCS"),sQuery(id+"F6.wireOp",EDGE,"E41.MirrorCS"),sQuery(id+"F6.wireOp",EDGE,"E42.MirrorCS"),sQuery(id+"F7.wireOp",EDGE,"E101.MirrorCS"),sQuery(id+"F7.wireOp",EDGE,"E102.MirrorCS"),sQuery(id+"F7.wireOp",EDGE,"E103.MirrorCS")])]})});
            var Q26;
            Q26=makeQuery(id+"F12.boolean.opBoolean","COPY",FACE,{"derivedFrom":makeQuery(id+"F12.opLoft","SWEPT_FACE",FACE,{"disambiguationData":[OSD([sQuery(id+"F6.wireOp",EDGE,"E38"),sQuery(id+"F6.wireOp",EDGE,"E41.MirrorCS"),sQuery(id+"F6.wireOp",EDGE,"E42.MirrorCS"),sQuery(id+"F7.wireOp",EDGE,"E99"),sQuery(id+"F7.wireOp",EDGE,"E102.MirrorCS"),sQuery(id+"F7.wireOp",EDGE,"E103.MirrorCS")])]})});
            var Q27;
            Q27=makeQuery(id+"F12.boolean.opBoolean","COPY",FACE,{"derivedFrom":makeQuery(id+"F12.opLoft","SWEPT_FACE",FACE,{"disambiguationData":[OSD([sQuery(id+"F6.wireOp",EDGE,"E35"),sQuery(id+"F6.wireOp",EDGE,"E37"),sQuery(id+"F6.wireOp",EDGE,"E38"),sQuery(id+"F7.wireOp",EDGE,"E97"),sQuery(id+"F7.wireOp",EDGE,"E98"),sQuery(id+"F7.wireOp",EDGE,"E99")])]})});
            var Q28;
            Q28=makeQuery(id+"F8.boolean.opBoolean","COPY",FACE,{"derivedFrom":makeQuery(id+"F8.opLoft","SWEPT_FACE",FACE,{"disambiguationData":[OSD([sQuery(id+"F6.wireOp",EDGE,"E28"),sQuery(id+"F6.wireOp",EDGE,"E31.MirrorCS"),sQuery(id+"F6.wireOp",EDGE,"E32.MirrorCS"),sQuery(id+"F7.wireOp",EDGE,"E77"),sQuery(id+"F7.wireOp",EDGE,"E80.MirrorCS"),sQuery(id+"F7.wireOp",EDGE,"E81.MirrorCS")])]})});
            var Q29;
            Q29=makeQuery(id+"F8.boolean.opBoolean","COPY",FACE,{"derivedFrom":makeQuery(id+"F8.opLoft","SWEPT_FACE",FACE,{"disambiguationData":[OSD([sQuery(id+"F6.wireOp",EDGE,"E30.MirrorCS"),sQuery(id+"F6.wireOp",EDGE,"E31.MirrorCS"),sQuery(id+"F6.wireOp",EDGE,"E32.MirrorCS"),sQuery(id+"F7.wireOp",EDGE,"E79.MirrorCS"),sQuery(id+"F7.wireOp",EDGE,"E80.MirrorCS"),sQuery(id+"F7.wireOp",EDGE,"E81.MirrorCS")])]})});
            var Q30;
            Q30=makeQuery(id+"F8.boolean.opBoolean","COPY",FACE,{"derivedFrom":makeQuery(id+"F8.opLoft","SWEPT_FACE",FACE,{"disambiguationData":[OSD([sQuery(id+"F6.wireOp",EDGE,"E29.MirrorCS"),sQuery(id+"F6.wireOp",EDGE,"E30.MirrorCS"),sQuery(id+"F6.wireOp",EDGE,"E31.MirrorCS"),sQuery(id+"F7.wireOp",EDGE,"E78.MirrorCS"),sQuery(id+"F7.wireOp",EDGE,"E79.MirrorCS"),sQuery(id+"F7.wireOp",EDGE,"E80.MirrorCS")])]})});
            var Q31;
            Q31=makeQuery(id+"F8.boolean.opBoolean","COPY",FACE,{"derivedFrom":makeQuery(id+"F8.opLoft","SWEPT_FACE",FACE,{"disambiguationData":[OSD([sQuery(id+"F6.wireOp",EDGE,"E26"),sQuery(id+"F6.wireOp",EDGE,"E29.MirrorCS"),sQuery(id+"F6.wireOp",EDGE,"E30.MirrorCS"),sQuery(id+"F7.wireOp",EDGE,"E74"),sQuery(id+"F7.wireOp",EDGE,"E78.MirrorCS"),sQuery(id+"F7.wireOp",EDGE,"E79.MirrorCS")])]})});
            var Q32;
            Q32=makeQuery(id+"F8.boolean.opBoolean","COPY",FACE,{"derivedFrom":makeQuery(id+"F8.opLoft","SWEPT_FACE",FACE,{"disambiguationData":[OSD([sQuery(id+"F6.wireOp",EDGE,"E25"),sQuery(id+"F6.wireOp",EDGE,"E26"),sQuery(id+"F6.wireOp",EDGE,"E29.MirrorCS"),sQuery(id+"F7.wireOp",EDGE,"E74"),sQuery(id+"F7.wireOp",EDGE,"E75"),sQuery(id+"F7.wireOp",EDGE,"E78.MirrorCS")])]})});
            var Q33;
            Q33=makeQuery(id+"F8.boolean.opBoolean","COPY",FACE,{"derivedFrom":makeQuery(id+"F8.opLoft","SWEPT_FACE",FACE,{"disambiguationData":[OSD([sQuery(id+"F6.wireOp",EDGE,"E25"),sQuery(id+"F6.wireOp",EDGE,"E26"),sQuery(id+"F6.wireOp",EDGE,"E27"),sQuery(id+"F7.wireOp",EDGE,"E74"),sQuery(id+"F7.wireOp",EDGE,"E75"),sQuery(id+"F7.wireOp",EDGE,"E76")])]})});
            var Q34;
            Q34=makeQuery(id+"F8.boolean.opBoolean","COPY",FACE,{"derivedFrom":makeQuery(id+"F8.opLoft","SWEPT_FACE",FACE,{"disambiguationData":[OSD([sQuery(id+"F6.wireOp",EDGE,"E25"),sQuery(id+"F6.wireOp",EDGE,"E27"),sQuery(id+"F6.wireOp",EDGE,"E28"),sQuery(id+"F7.wireOp",EDGE,"E75"),sQuery(id+"F7.wireOp",EDGE,"E76"),sQuery(id+"F7.wireOp",EDGE,"E77")])]})});
            fillet(context, id + "F15", {"entities" : qUnion([Q0, Q1, Q2, Q3, Q4, Q5, Q6, Q7, Q8, Q9, Q10, Q11, Q12, Q13, Q14, Q15, Q16, Q17, Q18, Q19, Q20, Q21, Q22, Q23, Q24, Q25, Q26, Q27, Q28, Q29, Q30, Q31, Q32, Q33, Q34]), "radius" : 3 * mm, "tangentPropagation" : true, "allowEdgeOverflow" : false});
        }
        {
            var Q0;
            Q0=qCreatedBy(makeId("Right.planeOp"),FACE);
            var sketch = newSketch(context, id + "F16", { "sketchPlane" : qUnion([Q0])});
            skLineSegment(sketch, "E134", {"start": v(-19.95, 38.55) * mm, "end": v(-18.71, 37.53) * mm});
            skLineSegment(sketch, "E135", {"start": v(-18.71, 37.53) * mm, "end": v(-16.47, 37.53) * mm});
            skLineSegment(sketch, "E136", {"start": v(-16.47, 37.53) * mm, "end": v(-13.38, 39.39) * mm});
            skLineSegment(sketch, "E137", {"start": v(-13.38, 39.39) * mm, "end": v(-3.7, 39.39) * mm});
            skLineSegment(sketch, "E138", {"start": v(-3.7, 39.39) * mm, "end": v(0, 42.98) * mm});
            skLineSegment(sketch, "E139", {"start": v(0, 42.98) * mm, "end": v(10.35, 42.98) * mm});
            skLineSegment(sketch, "E140", {"start": v(10.35, 42.98) * mm, "end": v(10.35, 0) * mm});
            skLineSegment(sketch, "E141", {"start": v(10.35, 0) * mm, "end": v(-36.04, 0) * mm});
            skLineSegment(sketch, "E142", {"start": v(-36.04, 0) * mm, "end": v(-36.04, 38.55) * mm});
            skLineSegment(sketch, "E143", {"start": v(-36.04, 38.55) * mm, "end": v(-19.95, 38.55) * mm});
            skSolve(sketch);
        }
        {
            var Q0;
            Q0 = qSketchRegion(id + "F16", true);
            var Q1;
            Q1=sQuery(id+"F16.wireOp",EDGE,"E141");
            revolve(context, id + "F17", {"operationType" : NewBodyOperationType.REMOVE, "entities" : qUnion([Q0]), "axis" : qUnion([Q1]), "revolveType" : RevolveType.FULL, "oppositeDirection" : true});
        }
        {
            var Q0;
            Q0=qCreatedBy(makeId("Front.planeOp"),FACE);
            var sketch = newSketch(context, id + "F18", { "sketchPlane" : qUnion([Q0])});
            skLineSegment(sketch, "E144.bottom", {"start": v(-61.51, 36.57) * mm, "end": v(121.32, 36.57) * mm});
            skLineSegment(sketch, "E144.top", {"start": v(-61.51, 5.22) * mm, "end": v(121.32, 5.22) * mm});
            skLineSegment(sketch, "E144.left", {"start": v(-61.51, 36.57) * mm, "end": v(-61.51, 5.22) * mm});
            skLineSegment(sketch, "E144.right", {"start": v(121.32, 36.57) * mm, "end": v(121.32, 5.22) * mm});
            skCircle(sketch, "E145", {"center": v(28.08, 20.11) * mm, "radius": 11.71 * mm});
            skSolve(sketch);
        }
        {
            var Q0;
            Q0=makeQuery(id+"F18.imprint","IMPRINT",FACE,{"disambiguationData":[TD([[makeQuery(id+"F18.imprint","IMPRINT",EDGE,{"derivedFrom":sQuery(id+"F18.wireOp",EDGE,"E144.bottom")}),-1.0]])]});
            extrude(context, id + "F19", {"entities" : qUnion([Q0]), "depth" : 25 * mm});
        }
    });
